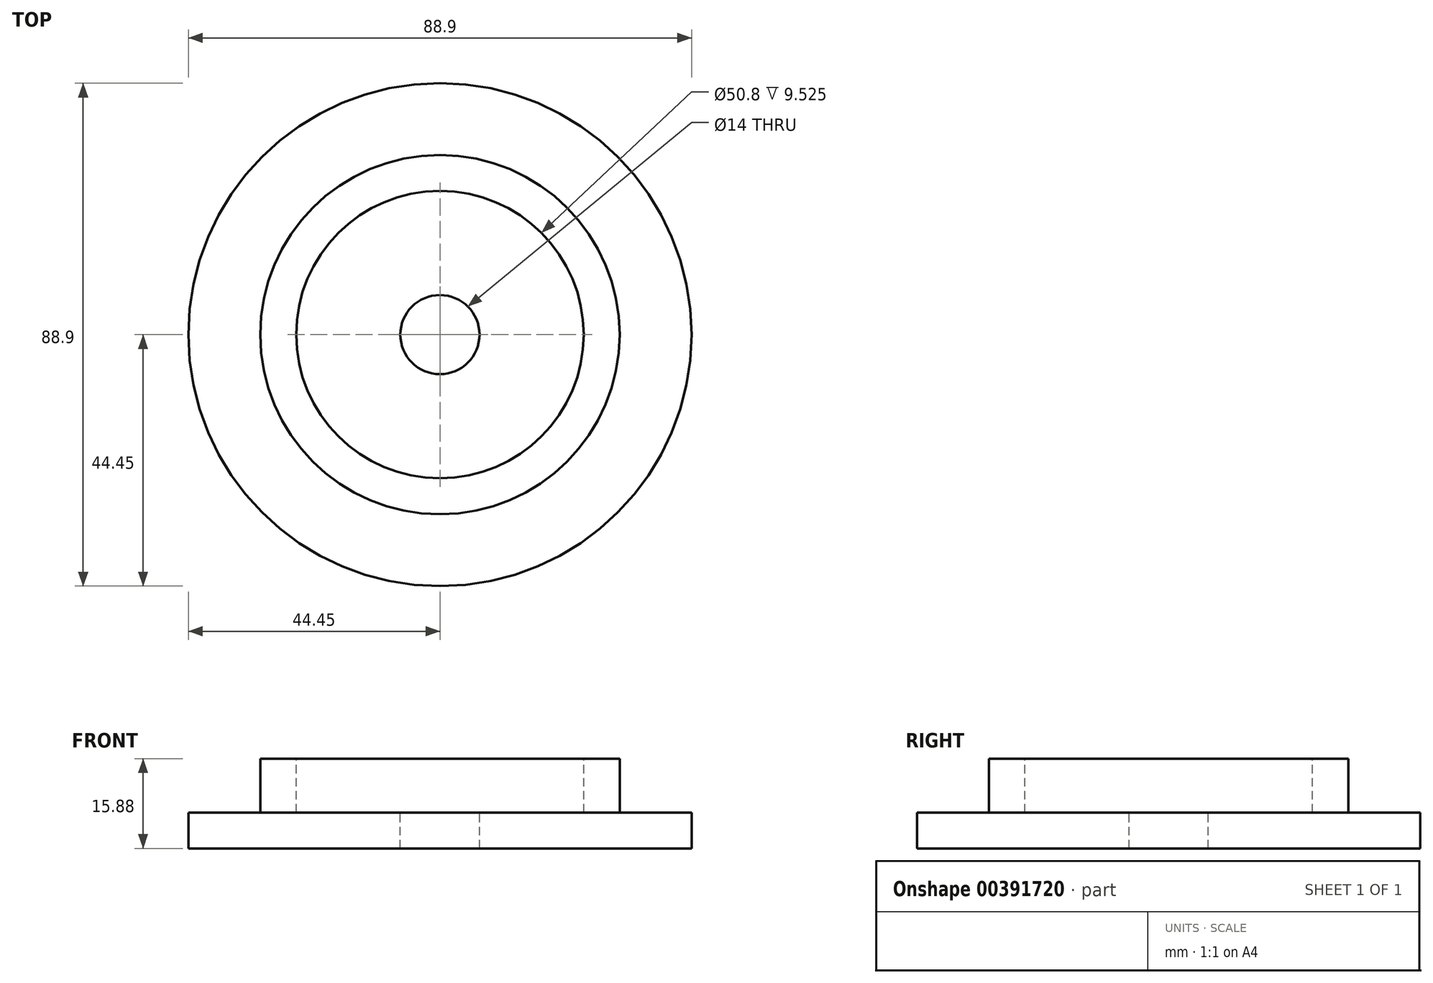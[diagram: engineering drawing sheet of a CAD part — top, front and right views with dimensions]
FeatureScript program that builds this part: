
annotation { "Feature Type Name" : "Feature", "Feature Type Description" : "" }
export const myFeature = defineFeature(function(context is Context, id is Id, definition is map)
    precondition{}
    {
        {
            var Q0;
            Q0=qCreatedBy(makeId("Front.planeOp"),FACE);
            var sketch = newSketch(context, id + "F0", { "sketchPlane" : qUnion([Q0])});
            skLineSegment(sketch, "E0", {"start": v(7, 0) * mm, "end": v(7, 6.35) * mm});
            skLineSegment(sketch, "E1", {"start": v(25.4, 15.87) * mm, "end": v(31.75, 15.87) * mm});
            skLineSegment(sketch, "E2", {"start": v(31.75, 15.87) * mm, "end": v(31.75, 6.35) * mm});
            skLineSegment(sketch, "E3", {"start": v(44.45, 6.35) * mm, "end": v(44.45, 0) * mm});
            skLineSegment(sketch, "E4", {"start": v(44.45, 0) * mm, "end": v(7, 0) * mm});
            skLineSegment(sketch, "E5", {"start": v(0, 44.3) * mm, "end": v(0, -45.73) * mm, "construction": true});
            skLineSegment(sketch, "E6", {"start": v(25.4, 15.87) * mm, "end": v(25.4, 6.35) * mm});
            skLineSegment(sketch, "E7", {"start": v(25.4, 6.35) * mm, "end": v(7, 6.35) * mm});
            skLineSegment(sketch, "E8", {"start": v(31.75, 6.35) * mm, "end": v(44.45, 6.35) * mm});
            skSolve(sketch);
        }
        {
            var Q0;
            Q0 = qSketchRegion(id + "F0", true);
            var Q1;
            Q1=sQuery(id+"F0.wireOp",EDGE,"E5");
            revolve(context, id + "F1", {"entities" : qUnion([Q0]), "axis" : qUnion([Q1]), "revolveType" : RevolveType.FULL});
        }
    });
